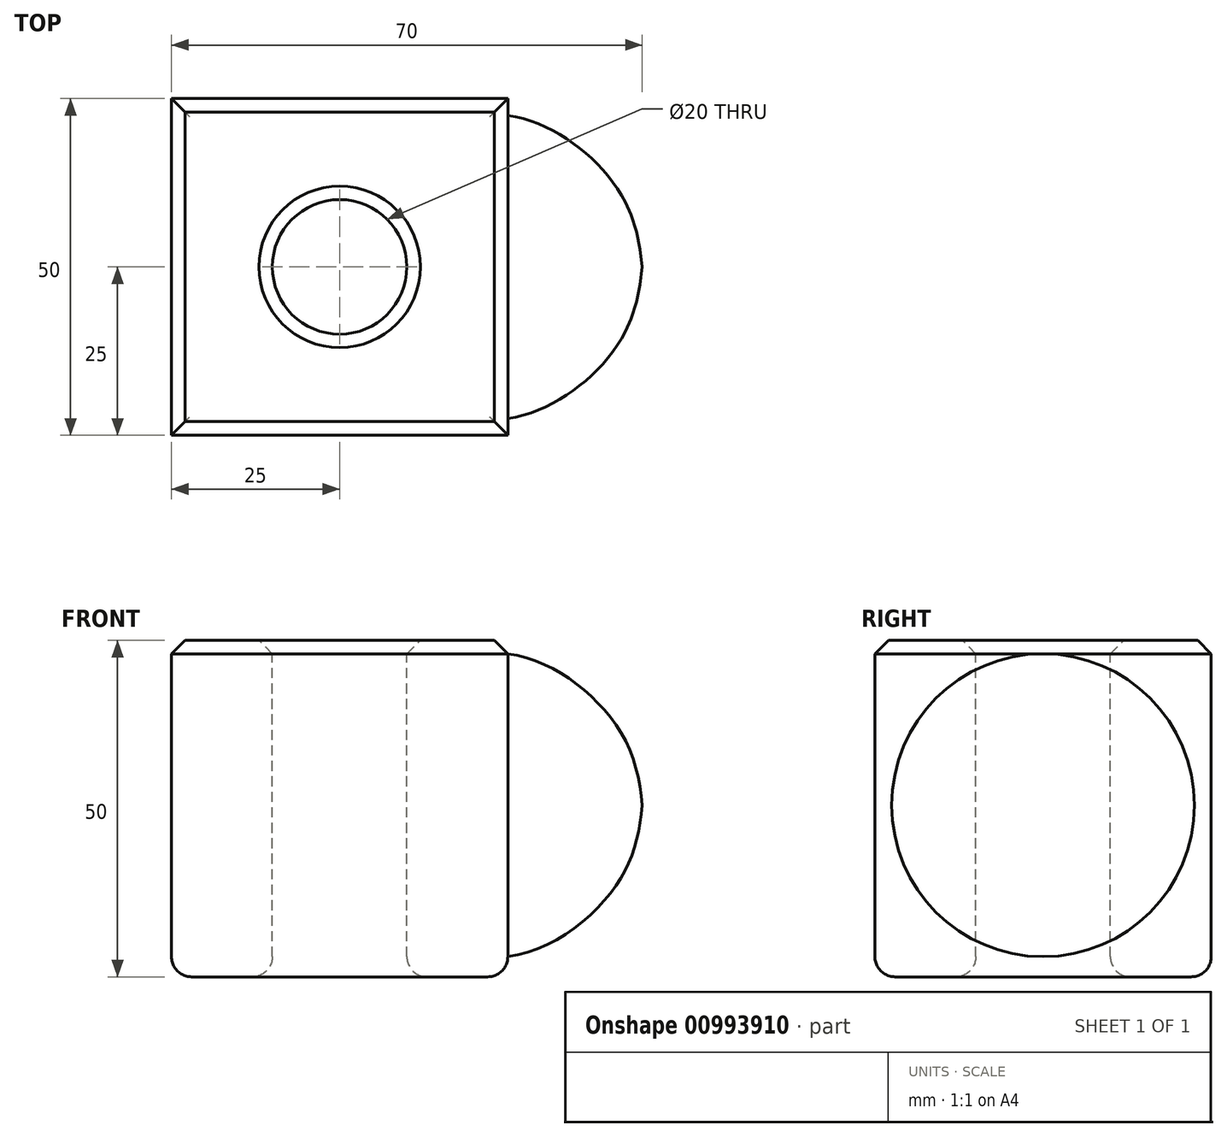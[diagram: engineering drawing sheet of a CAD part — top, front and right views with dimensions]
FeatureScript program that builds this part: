
annotation { "Feature Type Name" : "Feature", "Feature Type Description" : "" }
export const myFeature = defineFeature(function(context is Context, id is Id, definition is map)
    precondition{}
    {
        {
            var Q0;
            Q0=qCreatedBy(makeId("Top.planeOp"),FACE);
            var sketch = newSketch(context, id + "F0", { "sketchPlane" : qUnion([Q0])});
            skLineSegment(sketch, "E0.bottom", {"start": v(25, -25) * mm, "end": v(-25, -25) * mm});
            skLineSegment(sketch, "E0.top", {"start": v(25, 25) * mm, "end": v(-25, 25) * mm});
            skLineSegment(sketch, "E0.left", {"start": v(25, -25) * mm, "end": v(25, 25) * mm});
            skLineSegment(sketch, "E0.right", {"start": v(-25, -25) * mm, "end": v(-25, 25) * mm});
            skPoint(sketch, "E0.middle", {"position": v(0, 0) * mm});
            skSolve(sketch);
        }
        {
            var Q0;
            Q0=makeQuery(id+"F0.imprint","IMPRINT",FACE,{"disambiguationData":[TD([[makeQuery(id+"F0.imprint","IMPRINT",EDGE,{"derivedFrom":sQuery(id+"F0.wireOp",EDGE,"E0.bottom")}),-1.0]])]});
            extrude(context, id + "F1", {"entities" : qUnion([Q0]), "depth" : 50 * mm, "offsetDistance" : 25 * mm});
        }
        {
            var Q0;
            Q0=makeQuery(id+"F1.opExtrude","CAP_FACE",FACE,{"disambiguationData":[OSD([sQuery(id+"F0.wireOp",EDGE,"E0.bottom"),sQuery(id+"F0.wireOp",EDGE,"E0.top"),sQuery(id+"F0.wireOp",EDGE,"E0.left"),sQuery(id+"F0.wireOp",EDGE,"E0.right")])],"isStart":false});
            var sketch = newSketch(context, id + "F2", { "sketchPlane" : qUnion([Q0])});
            skCircle(sketch, "E1", {"center": v(0, 0) * mm, "radius": 10 * mm});
            skSolve(sketch);
        }
        {
            var Q0;
            Q0=makeQuery(id+"F2.imprint","IMPRINT",FACE,{"disambiguationData":[TD([[makeQuery(id+"F2.imprint","IMPRINT",EDGE,{"derivedFrom":sQuery(id+"F2.wireOp",EDGE,"E1")}),1.0]])]});
            extrude(context, id + "F3", {"entities" : qUnion([Q0]), "operationType" : NewBodyOperationType.REMOVE, "endBound" : BoundingType.THROUGH_ALL, "oppositeDirection" : true, "depth" : 50 * mm, "offsetDistance" : 25 * mm});
        }
        {
            var Q0;
            Q0=makeQuery(id+"F1.opExtrude","CAP_FACE",FACE,{"disambiguationData":[OSD([sQuery(id+"F0.wireOp",EDGE,"E0.bottom"),sQuery(id+"F0.wireOp",EDGE,"E0.top"),sQuery(id+"F0.wireOp",EDGE,"E0.left"),sQuery(id+"F0.wireOp",EDGE,"E0.right")])],"isStart":false});
            chamfer(context, id + "F4", {"entities" : qUnion([Q0]), "width" : 2 * mm, "tangentPropagation" : true});
        }
        {
            var Q0;
            Q0=makeQuery(id+"F1.opExtrude","CAP_FACE",FACE,{"disambiguationData":[OSD([sQuery(id+"F0.wireOp",EDGE,"E0.bottom"),sQuery(id+"F0.wireOp",EDGE,"E0.top"),sQuery(id+"F0.wireOp",EDGE,"E0.left"),sQuery(id+"F0.wireOp",EDGE,"E0.right")])],"isStart":true});
            fillet(context, id + "F5", {"entities" : qUnion([Q0]), "radius" : 3 * mm, "tangentPropagation" : true, "allowEdgeOverflow" : false});
        }
        {
            var Q0;
            Q0=qCreatedBy(makeId("Front.planeOp"),FACE);
            var sketch = newSketch(context, id + "F6", { "sketchPlane" : qUnion([Q0])});
            skLineSegment(sketch, "E2.0", {"start": v(25, 25.5) * mm, "end": v(25, 3) * mm});
            skLineSegment(sketch, "E3", {"start": v(25, 25.5) * mm, "end": v(45, 25.5) * mm});
            skFitSpline(sketch, "E4", {"points": [v(45, 25.5) * mm, v(40.63, 12.93) * mm, v(25, 3) * mm], "startDerivative": vector(-3.1, -31.28) * mm, "endDerivative": vector(-34.63, -4.3) * mm});
            skPoint(sketch, "E5.orphan", {"position": v(25, 48) * mm});
            skSolve(sketch);
        }
        {
            var Q0;
            Q0=makeQuery(id+"F6.imprint","IMPRINT",FACE,{"disambiguationData":[TD([[makeQuery(id+"F6.imprint","IMPRINT",EDGE,{"derivedFrom":sQuery(id+"F6.wireOp",EDGE,"E2.0")}),1.0]])]});
            var Q1;
            Q1=sQuery(id+"F6.wireOp",EDGE,"E3");
            revolve(context, id + "F7", {"operationType" : NewBodyOperationType.ADD, "surfaceOperationType" : NewSurfaceOperationType.NEW, "entities" : qUnion([Q0]), "axis" : qUnion([Q1]), "revolveType" : RevolveType.FULL});
        }
    });
